# Revit family: 306_1b426d89d2874f46ad528179ebd04e
name_source: partatom
category: Pipe Accessories
units: mm (PartAtom-declared; Revit-internal decimal feet)

## family parameters
Always vertical = Yes
Cut with Voids When Loaded = No
Part Type = Valve - Breaks Into
Round Connector Dimension = Use Diameter
Shared = No
Work Plane-Based = No

## types (2) — shared parameters
B = 54 mm  [stored 0.177165 ft]
C = 52 mm  [stored 0.170604 ft]
CAT0 = Yes
CT2 = 21 mm
Description = Thermostatic mixing valve VTA332, PN10 external thread
L2D = 56 mm
L2D_Min = 3048 mm  [stored 10 ft]
LT2 = 28 mm  [stored 0.0918635 ft]
MC = No
Manufacturer = ESBE
QmdConnectorList = 301;D;302;D
URL = http://www.esbe.eu
W1 = 17 mm
WT2 = 23 mm  [stored 0.0754593 ft]
X1 = 2 mm  [stored 0.00656168 ft]
X2 = 7 mm  [stored 0.0229659 ft]
X3 = 52 mm  [stored 0.170604 ft]
X4 = 48 mm  [stored 0.15748 ft]
magiPartTypeId = 306
magiProductFamilyId = 1b426d89d2874f46ad528179ebd04e

## per-type parameters (varying)
| type | A | A__ve | D | DT2 | R2 | W2D | Z1 | Z1__ve | Z2 | magiProductId |
| VTA332 35-60°C 20-1,2 G3/4 | 30 mm  [stored 0.0984252 ft] | -30 mm  [stored -0.0984252 ft] | 20 mm | 10 mm  [stored 0.0328084 ft] | 9 mm  [stored 0.0295276 ft] | 20 mm  [stored 0.0656168 ft] | 26 mm  [stored 0.0853018 ft] | -26 mm  [stored -0.0853018 ft] | 9 mm  [stored 0.0295276 ft] | 91d1eeeadd4446bbb844fc4184a826 |
| VTA332 35-60°C 20-1,3 G1 | 32 mm | -32 mm | 25 mm | 13 mm  [stored 0.0426509 ft] | 11 mm  [stored 0.0360892 ft] | 25 mm  [stored 0.082021 ft] | 24 mm  [stored 0.0787402 ft] | -24 mm  [stored -0.0787402 ft] | 8 mm  [stored 0.0262467 ft] | 880d0742d20447178deeb757c69916 |

note: column(s) folded — value = type name in every type: magiProductCode

note: [stored X ft] marks values corroborated as IEEE doubles in the binary element streams (Revit-internal decimal feet)

## geometry (parser evidence)
native form markers: Sweep x1
no freeform markers — native parametric forms only
